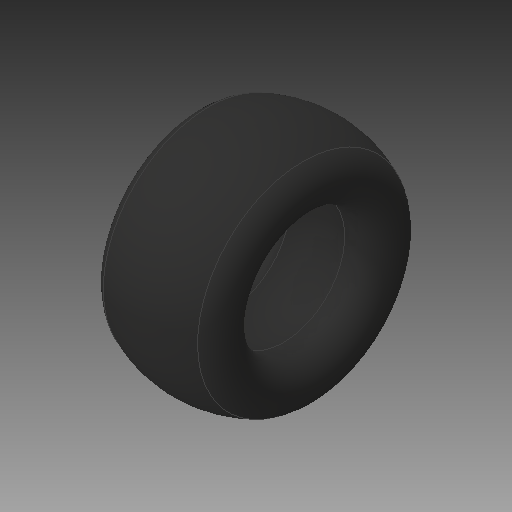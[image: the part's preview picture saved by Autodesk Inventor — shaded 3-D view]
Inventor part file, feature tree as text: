
AUTODESK INVENTOR PART (.ipt)
format: ipt  version: 2019 (Build 230136000, 136)  size: 194,560 bytes
history: native  units: mm
features: sketch x2, other x1, sweep x1
ambient origin geometry x8: Origin, YZ Plane, XZ Plane, XY Plane, X Axis, Y Axis, Z Axis, Center Point
bodies: Body1 (feature_tree)
feature tree (4):
  other  "Твердое тело1"
  sweep  "Сдвиг1"
  sketch  "Эскиз1"
  sketch  "Эскиз2"
